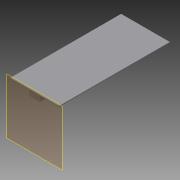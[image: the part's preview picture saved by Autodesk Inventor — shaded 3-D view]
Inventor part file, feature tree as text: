
AUTODESK INVENTOR PART (.ipt)
format: ipt  version: 2014 (Build 180170000, 170)  size: 93,696 bytes
history: native  units: in
note: dims shown in document units (in); Inventor stores cm internally (conversion verified against a paired STEP export)
features: plane x1, extrude x1, sketch x1, reference x1
ambient origin geometry x8: Origin, YZ Plane, XZ Plane, XY Plane, X Axis, Y Axis, Z Axis, Center Point
bodies: Solid1 (feature_tree)
feature tree (4):
  plane  "Work Plane1"
  extrude  "Extrusion1"  Depth=3.3in
  sketch  "Sketch1"  dims[d0=0.025in d1=0.025in d2=0.001in d3=0.0236in d4=0.01in d5=0.01in d6=0.001in d7=3.3in d8=0.0in]
  reference  "Reference1"
